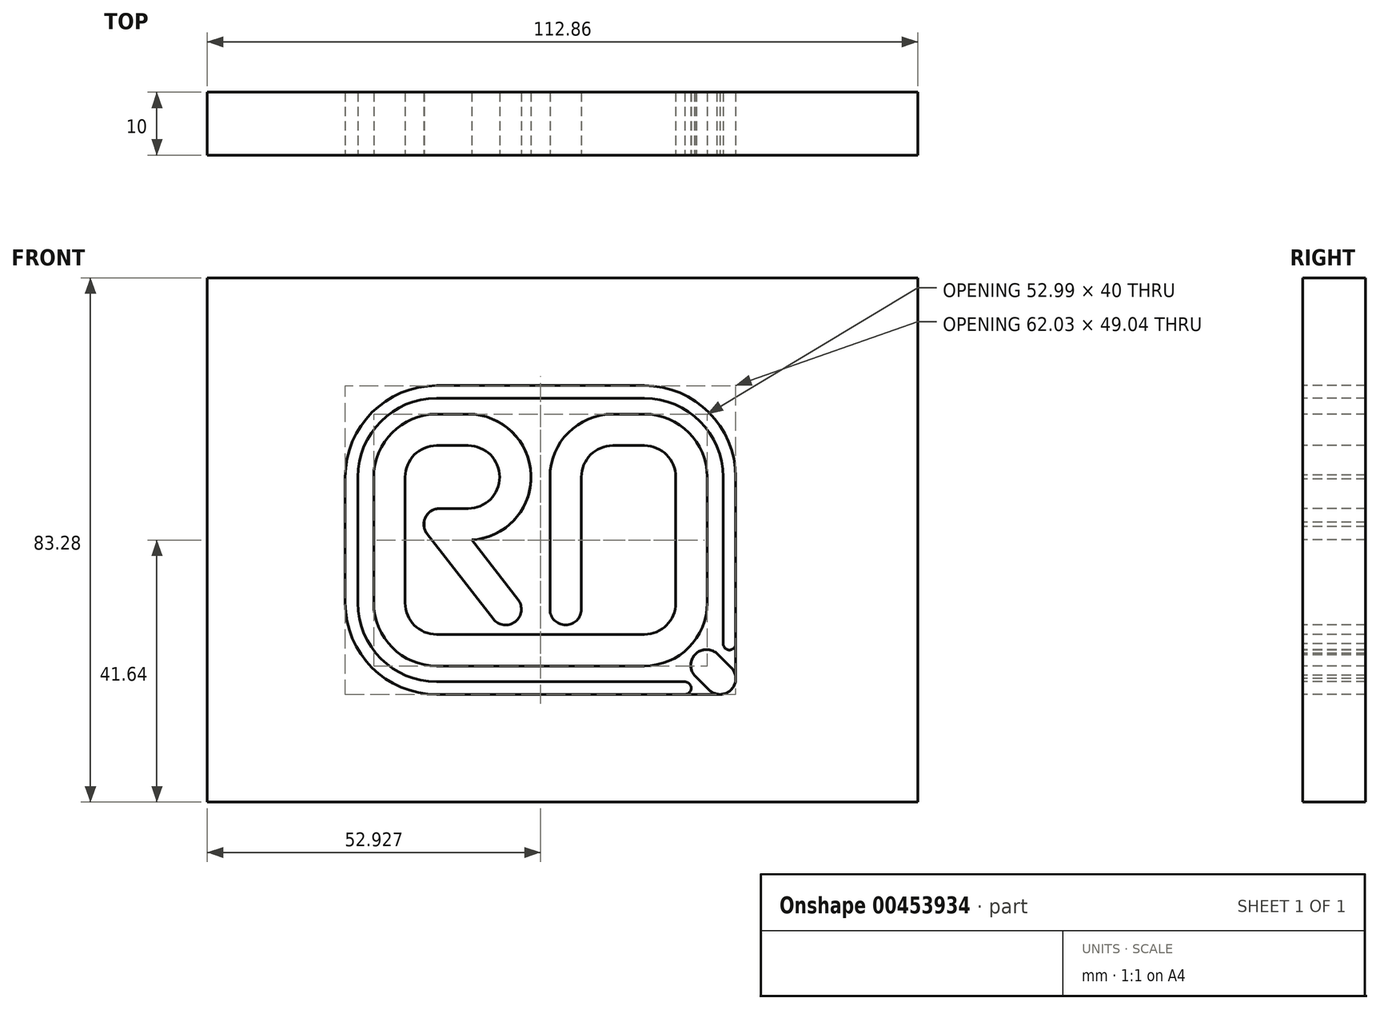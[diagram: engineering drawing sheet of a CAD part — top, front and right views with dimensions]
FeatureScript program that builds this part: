
annotation { "Feature Type Name" : "Feature", "Feature Type Description" : "" }
export const myFeature = defineFeature(function(context is Context, id is Id, definition is map)
    precondition{}
    {
        {
            var Q0;
            Q0=qCreatedBy(makeId("Front.planeOp"),FACE);
            var sketch = newSketch(context, id + "F0", { "sketchPlane" : qUnion([Q0])});
            skPoint(sketch, "E0.middle", {"position": v(0, 0) * mm});
            skLineSegment(sketch, "E1", {"start": v(-25, 10) * mm, "end": v(-25, -10) * mm});
            skLineSegment(sketch, "E2", {"start": v(-2, -20) * mm, "end": v(-0.38, -20) * mm});
            skLineSegment(sketch, "E3", {"start": v(-2, -11) * mm, "end": v(-2, 10) * mm});
            skLineSegment(sketch, "E4", {"start": v(8, 20) * mm, "end": v(13, 20) * mm});
            skLineSegment(sketch, "E5", {"start": v(23, 10) * mm, "end": v(23, -10) * mm});
            skLineSegment(sketch, "E6", {"start": v(13, -20) * mm, "end": v(9, -20) * mm});
            skLineSegment(sketch, "E7", {"start": v(-25, 20) * mm, "end": v(-15, 20) * mm});
            skLineSegment(sketch, "E8", {"start": v(-21, 0) * mm, "end": v(-15, 0) * mm, "construction": true});
            skLineSegment(sketch, "E9", {"start": v(-5, 10.33) * mm, "end": v(-5, 10.33) * mm});
            skPoint(sketch, "E10.visualSharp", {"position": v(-5.33, 20) * mm});
            skArc(sketch, "E10.filletArc", {"start": v(-5, 10.33) * mm, "mid": v(-8.05, 17.19) * mm, "end": v(-15, 20) * mm});
            skArc(sketch, "E11.filletArc", {"start": v(-15, 0) * mm, "mid": v(-7.81, 3.05) * mm, "end": v(-5, 10.33) * mm});
            skPoint(sketch, "E12.visualSharp", {"position": v(-3.63, -20) * mm});
            skPoint(sketch, "E13.visualSharp", {"position": v(23, -20) * mm});
            skArc(sketch, "E13.filletArc", {"start": v(13, -20) * mm, "mid": v(20.07, -17.07) * mm, "end": v(23, -10) * mm});
            skPoint(sketch, "E14.visualSharp", {"position": v(23, 20) * mm});
            skArc(sketch, "E14.filletArc", {"start": v(23, 10) * mm, "mid": v(20.07, 17.07) * mm, "end": v(13, 20) * mm});
            skPoint(sketch, "E15.visualSharp", {"position": v(-2, 20) * mm});
            skArc(sketch, "E15.filletArc", {"start": v(8, 20) * mm, "mid": v(0.92, 17.07) * mm, "end": v(-2, 10) * mm});
            skPoint(sketch, "E16.visualSharp", {"position": v(-2, -20) * mm});
            skArc(sketch, "E17.0", {"start": v(8, 15) * mm, "mid": v(4.46, 13.54) * mm, "end": v(3, 10) * mm});
            skLineSegment(sketch, "E17.1", {"start": v(3, -11) * mm, "end": v(3, 10) * mm});
            skLineSegment(sketch, "E17.2", {"start": v(8, 15) * mm, "end": v(13, 15) * mm});
            skArc(sketch, "E17.4", {"start": v(18, 10) * mm, "mid": v(16.53, 13.54) * mm, "end": v(13, 15) * mm});
            skLineSegment(sketch, "E17.5", {"start": v(18, 10) * mm, "end": v(18, -10) * mm});
            skArc(sketch, "E17.6", {"start": v(13, -15) * mm, "mid": v(16.53, -13.54) * mm, "end": v(18, -10) * mm});
            skLineSegment(sketch, "E17.7", {"start": v(13, -15) * mm, "end": v(9, -15) * mm});
            skArc(sketch, "E18.1", {"start": v(-15, 5) * mm, "mid": v(-11.44, 6.5) * mm, "end": v(-10, 10.08) * mm});
            skArc(sketch, "E18.2", {"start": v(-10, 10.08) * mm, "mid": v(-11.5, 13.56) * mm, "end": v(-15, 15) * mm});
            skLineSegment(sketch, "E18.3", {"start": v(-20, 15) * mm, "end": v(-15, 15) * mm});
            skLineSegment(sketch, "E19.0", {"start": v(-30, 17.5) * mm, "end": v(-30, -10) * mm});
            skLineSegment(sketch, "E20.0", {"start": v(-1, -15) * mm, "end": v(-0.38, -15) * mm});
            skLineSegment(sketch, "E21", {"start": v(-20, -20) * mm, "end": v(-2, -20) * mm});
            skLineSegment(sketch, "E22", {"start": v(-1, -15) * mm, "end": v(9, -15) * mm});
            skLineSegment(sketch, "E23.0", {"start": v(-20, -15) * mm, "end": v(0, -15) * mm});
            skLineSegment(sketch, "E24", {"start": v(-5, 10.33) * mm, "end": v(-5, 0) * mm});
            skLineSegment(sketch, "E25", {"start": v(0.5, -13.5) * mm, "end": v(0.5, -13.5) * mm});
            skPoint(sketch, "E26.visualSharp", {"position": v(3, -13.5) * mm});
            skArc(sketch, "E26.filletArc", {"start": v(0.5, -13.5) * mm, "mid": v(2.26, -12.77) * mm, "end": v(3, -11) * mm});
            skPoint(sketch, "E27.newPointB", {"position": v(-23.5, -13.5) * mm});
            skArc(sketch, "E27.filletArc", {"start": v(-2, -11) * mm, "mid": v(-1.27, -12.77) * mm, "end": v(0.5, -13.5) * mm});
            skPoint(sketch, "E28.visualSharp", {"position": v(-30, -20) * mm});
            skArc(sketch, "E28.filletArc", {"start": v(-30, -19.5) * mm, "mid": v(-29.85, -19.85) * mm, "end": v(-29.5, -20) * mm});
            skLineSegment(sketch, "E29", {"start": v(-7.28, -12.77) * mm, "end": v(-7.28, -12.77) * mm});
            skArc(sketch, "E30.filletArc", {"start": v(-7.28, -12.77) * mm, "mid": v(-6.55, -11) * mm, "end": v(-7.27, -9.24) * mm});
            skArc(sketch, "E31.filletArc", {"start": v(-11.23, -12.21) * mm, "mid": v(-9.4, -13.48) * mm, "end": v(-7.28, -12.77) * mm});
            skLineSegment(sketch, "E32.0", {"start": v(19.16, -19.7) * mm, "end": v(23.25, -23.79) * mm});
            skLineSegment(sketch, "E33.0", {"start": v(14.76, -15.3) * mm, "end": v(14.29, -14.83) * mm});
            skPoint(sketch, "E34.newPointB", {"position": v(-25, 20) * mm});
            skPoint(sketch, "E35.visualSharp", {"position": v(-23.5, 5) * mm});
            skPoint(sketch, "E36.visualSharp", {"position": v(-23.5, 0) * mm});
            skLineSegment(sketch, "E37", {"start": v(-30, 10) * mm, "end": v(-30, 17.5) * mm});
            skLineSegment(sketch, "E38", {"start": v(-20, 20) * mm, "end": v(-25, 20) * mm});
            skPoint(sketch, "E39.visualSharp", {"position": v(-30, 20) * mm});
            skArc(sketch, "E39.filletArc", {"start": v(-20, 20) * mm, "mid": v(-27.07, 17.07) * mm, "end": v(-30, 10) * mm});
            skArc(sketch, "E40", {"start": v(23.25, -23.79) * mm, "mid": v(26.79, -23.79) * mm, "end": v(26.78, -20.25) * mm});
            skPoint(sketch, "E41", {"position": v(20.07, -17.07) * mm});
            skPoint(sketch, "E42.orphan", {"position": v(16.53, -13.54) * mm});
            skLineSegment(sketch, "E43.trimOffspring", {"start": v(13, -20) * mm, "end": v(-0.38, -20) * mm});
            skArc(sketch, "E44.trimOffspring", {"start": v(19.16, -19.7) * mm, "mid": v(21.12, -18.14) * mm, "end": v(22.69, -16.19) * mm});
            skPoint(sketch, "E45.newPointB", {"position": v(-25, -20) * mm});
            skArc(sketch, "E45.filletArc", {"start": v(-25, -10) * mm, "mid": v(-23.54, -13.54) * mm, "end": v(-20, -15) * mm});
            skLineSegment(sketch, "E46", {"start": v(-15, 20) * mm, "end": v(8, 20) * mm});
            skLineSegment(sketch, "E47", {"start": v(21.86, -24.52) * mm, "end": v(-20, -24.52) * mm});
            skLineSegment(sketch, "E48", {"start": v(27.51, -22.02) * mm, "end": v(27.51, -18.87) * mm});
            skLineSegment(sketch, "E49", {"start": v(13, 24.52) * mm, "end": v(-20, 24.52) * mm});
            skLineSegment(sketch, "E50", {"start": v(-34.52, -10) * mm, "end": v(-34.52, 10) * mm});
            skPoint(sketch, "E51.orphan", {"position": v(17.43, -17.97) * mm});
            skPoint(sketch, "E52.orphan", {"position": v(13.35, -13.89) * mm});
            skArc(sketch, "E53.0", {"start": v(27.51, 10) * mm, "mid": v(23.26, 20.27) * mm, "end": v(13, 24.52) * mm});
            skArc(sketch, "E54.0", {"start": v(25.51, 10) * mm, "mid": v(21.85, 18.85) * mm, "end": v(13, 22.52) * mm});
            skLineSegment(sketch, "E55.0", {"start": v(25.51, -22.07) * mm, "end": v(25.51, -19) * mm});
            skLineSegment(sketch, "E56.0", {"start": v(25.02, -22.52) * mm, "end": v(21.98, -22.52) * mm});
            skLineSegment(sketch, "E57.0", {"start": v(-32.52, -10) * mm, "end": v(-32.52, 10) * mm});
            skLineSegment(sketch, "E58.0", {"start": v(13, 22.52) * mm, "end": v(-20, 22.52) * mm});
            skPoint(sketch, "E59.visualSharp", {"position": v(-32.52, 22.52) * mm});
            skArc(sketch, "E59.filletArc", {"start": v(-20, 22.52) * mm, "mid": v(-28.85, 18.85) * mm, "end": v(-32.52, 10) * mm});
            skArc(sketch, "E60.0", {"start": v(-20, 24.52) * mm, "mid": v(-30.27, 20.27) * mm, "end": v(-34.52, 10) * mm});
            skPoint(sketch, "E61.visualSharp", {"position": v(-32.52, -22.52) * mm});
            skLineSegment(sketch, "E62", {"start": v(26.51, -15) * mm, "end": v(26.51, -16.32) * mm});
            skLineSegment(sketch, "E63.0", {"start": v(18.1, -20.77) * mm, "end": v(22.19, -24.85) * mm, "construction": true});
            skLineSegment(sketch, "E64.0", {"start": v(23.75, -15.12) * mm, "end": v(27.84, -19.2) * mm, "construction": true});
            skArc(sketch, "E65", {"start": v(19.44, -24.52) * mm, "mid": v(20.44, -23.52) * mm, "end": v(19.44, -22.52) * mm});
            skArc(sketch, "E66", {"start": v(25.51, -16.47) * mm, "mid": v(26.51, -17.47) * mm, "end": v(27.51, -16.47) * mm});
            skLineSegment(sketch, "E67.trimOffspring", {"start": v(25.51, -14) * mm, "end": v(25.51, 10) * mm});
            skLineSegment(sketch, "E68.trimOffspring", {"start": v(27.51, -14) * mm, "end": v(27.51, 33) * mm});
            skLineSegment(sketch, "E69.trimOffspring", {"start": v(19.86, -22.52) * mm, "end": v(-20, -22.52) * mm});
            skLineSegment(sketch, "E70", {"start": v(21.86, -24.52) * mm, "end": v(25.02, -24.52) * mm});
            skLineSegment(sketch, "E71", {"start": v(27.51, -14) * mm, "end": v(27.51, -22.02) * mm});
            skLineSegment(sketch, "E72.bottom", {"start": v(-56.43, 41.64) * mm, "end": v(56.43, 41.64) * mm});
            skLineSegment(sketch, "E72.top", {"start": v(-56.43, -41.64) * mm, "end": v(56.43, -41.64) * mm});
            skLineSegment(sketch, "E72.left", {"start": v(-56.43, 41.64) * mm, "end": v(-56.43, -41.64) * mm});
            skLineSegment(sketch, "E72.right", {"start": v(56.43, 41.64) * mm, "end": v(56.43, -41.64) * mm});
            skLineSegment(sketch, "E73", {"start": v(0, 0) * mm, "end": v(0, -38.7) * mm, "construction": true});
            skLineSegment(sketch, "E74", {"start": v(0, 0) * mm, "end": v(33.56, 0) * mm, "construction": true});
            skArc(sketch, "E75.filletArc", {"start": v(-20, 15) * mm, "mid": v(-23.54, 13.54) * mm, "end": v(-25, 10) * mm});
            skArc(sketch, "E76.0", {"start": v(-30, -10) * mm, "mid": v(-27.07, -17.07) * mm, "end": v(-20, -20) * mm});
            skArc(sketch, "E77.0", {"start": v(-34.52, -10) * mm, "mid": v(-30.27, -20.27) * mm, "end": v(-20, -24.52) * mm});
            skArc(sketch, "E78.0", {"start": v(-32.52, -10) * mm, "mid": v(-28.85, -18.85) * mm, "end": v(-20, -22.52) * mm});
            skLineSegment(sketch, "E79", {"start": v(-15, 5) * mm, "end": v(-21, 5) * mm});
            skLineSegment(sketch, "E80", {"start": v(-23.5, 2.5) * mm, "end": v(-23.5, 2.5) * mm});
            skPoint(sketch, "E81.startSnap0", {"position": v(-6.55, -11) * mm});
            skArc(sketch, "E82.0", {"start": v(13, -22.52) * mm, "mid": v(21.85, -18.85) * mm, "end": v(25.51, -10) * mm});
            skArc(sketch, "E83", {"start": v(24.48, -17.98) * mm, "mid": v(21.11, -18.13) * mm, "end": v(20.96, -21.5) * mm});
            skLineSegment(sketch, "E84", {"start": v(24.48, -17.98) * mm, "end": v(26.78, -20.25) * mm});
            skLineSegment(sketch, "E85", {"start": v(25.51, -16.47) * mm, "end": v(25.51, -14) * mm});
            skLineSegment(sketch, "E86", {"start": v(-22, 7.18) * mm, "end": v(-22, -5.45) * mm});
            skArc(sketch, "E87", {"start": v(-19.53, 5) * mm, "mid": v(-22.03, 2.5) * mm, "end": v(-19.53, 0) * mm});
            skLineSegment(sketch, "E88", {"start": v(-21.5, 0.97) * mm, "end": v(-11.02, -12.53) * mm});
            skLineSegment(sketch, "E89.0", {"start": v(-17.54, 4.02) * mm, "end": v(-7.07, -9.47) * mm});
            skSolve(sketch);
        }
        {
            var Q0;
            Q0=makeQuery(id+"F0.imprint","IMPRINT",FACE,{"disambiguationData":[TD([[makeQuery(id+"F0.imprint","IMPRINT",EDGE,{"derivedFrom":sQuery(id+"F0.wireOp",EDGE,"E1")}),-1.0]])]});
            var Q1;
            {var subQ6=sQuery(id+"F0.wireOp",EDGE,"8dgEX87s-OnN3-UPAw-RyUf-tcfM0RuKeMZf");Q1=makeQuery(id+"F0.imprint","IMPRINT",FACE,{"disambiguationData":[TD([[makeQuery(id+"F0.imprint","IMPRINT",EDGE,{"derivedFrom":subQ6}),1.0]])]});}
            var Q2;
            {var subQ0=sQuery(id+"F0.wireOp",EDGE,"E40");var subQ1=makeQuery(id+"F0.imprint","INTERSECT",VERTEX,{"derivedFrom":[sQuery(id+"F0.wireOp",EDGE,"c0c087a9-fd36-4214-a694-875f0f01d769.0"),subQ0]});Q2=makeQuery(id+"F0.imprint","IMPRINT",FACE,{"disambiguationData":[TD([[makeQuery(id+"F0.imprint","IMPRINT",EDGE,{"disambiguationData":[TD([[subQ1,-1.0]])],"derivedFrom":subQ0}),1.0]])]});}
            var Q3;
            {var subQ0=sQuery(id+"F0.wireOp",EDGE,"E0.bottom");Q3=makeQuery(id+"F0.imprint","IMPRINT",FACE,{"disambiguationData":[TD([[makeQuery(id+"F0.imprint","IMPRINT",EDGE,{"derivedFrom":subQ0}),-1.0]])]});}
            var Q4;
            {var subQ0=sQuery(id+"F0.wireOp",EDGE,"E0.bottom");Q4=makeQuery(id+"F0.imprint","IMPRINT",FACE,{"disambiguationData":[TD([[makeQuery(id+"F0.imprint","IMPRINT",EDGE,{"derivedFrom":subQ0}),1.0]])]});}
            var Q5;
            {var subQ0=sQuery(id+"F0.wireOp",EDGE,"E31.filletArc");Q5=makeQuery(id+"F0.imprint","IMPRINT",FACE,{"disambiguationData":[TD([[makeQuery(id+"F0.imprint","IMPRINT",EDGE,{"derivedFrom":subQ0}),1.0]])]});}
            var Q6;
            {var subQ0=sQuery(id+"F0.wireOp",EDGE,"E83");var subQ1=sQuery(id+"F0.wireOp",EDGE,"E44.trimOffspring");var subQ2=makeQuery(id+"F0.imprint","INTERSECT",VERTEX,{"disambiguationData":[OD(0.0)],"derivedFrom":[subQ1,subQ0]});Q6=makeQuery(id+"F0.imprint","IMPRINT",FACE,{"disambiguationData":[TD([[makeQuery(id+"F0.imprint","IMPRINT",EDGE,{"disambiguationData":[TD([[subQ2,-1.0]])],"derivedFrom":subQ1}),-1.0]])]});}
            var Q7;
            {var subQ6=sQuery(id+"F0.wireOp",EDGE,"E32.0");var subQ8=makeQuery(id+"F0.imprint","IMPRINT",VERTEX,{"derivedFrom":subQ6});Q7=makeQuery(id+"F0.imprint","IMPRINT",FACE,{"disambiguationData":[TD([[makeQuery(id+"F0.imprint","IMPRINT",EDGE,{"disambiguationData":[TD([[subQ8,1.0]])],"derivedFrom":subQ6}),1.0]])]});}
            var Q8;
            {var subQ0=sQuery(id+"F0.wireOp",EDGE,"E83");var subQ1=sQuery(id+"F0.wireOp",EDGE,"E44.trimOffspring");var subQ2=makeQuery(id+"F0.imprint","INTERSECT",VERTEX,{"disambiguationData":[OD(0.0)],"derivedFrom":[subQ1,subQ0]});Q8=makeQuery(id+"F0.imprint","IMPRINT",FACE,{"disambiguationData":[TD([[makeQuery(id+"F0.imprint","IMPRINT",EDGE,{"disambiguationData":[TD([[subQ2,1.0]])],"derivedFrom":subQ1}),-1.0]])]});}
            extrude(context, id + "F1", {"entities" : qUnion([Q0, Q1, Q2, Q3, Q4, Q5, Q6, Q7, Q8]), "oppositeDirection" : true, "depth" : 10 * mm});
        }
        {
            var Q0;
            Q0=makeQuery(id+"F0.imprint","IMPRINT",FACE,{"disambiguationData":[TD([[makeQuery(id+"F0.imprint","IMPRINT",EDGE,{"derivedFrom":sQuery(id+"F0.wireOp",EDGE,"E1")}),1.0]])]});
            var Q1;
            {var subQ16=sQuery(id+"F0.wireOp",EDGE,"E2");Q1=makeQuery(id+"F0.imprint","IMPRINT",FACE,{"disambiguationData":[TD([[makeQuery(id+"F0.imprint","IMPRINT",EDGE,{"derivedFrom":subQ16}),-1.0]])]});}
            var Q2;
            {var subQ10=sQuery(id+"F0.wireOp",EDGE,"E65");Q2=makeQuery(id+"F0.imprint","IMPRINT",FACE,{"disambiguationData":[TD([[makeQuery(id+"F0.imprint","IMPRINT",EDGE,{"derivedFrom":subQ10}),-1.0]])]});}
            var Q3;
            {var subQ0=sQuery(id+"F0.wireOp",EDGE,"E44.trimOffspring");var subQ1=sQuery(id+"F0.wireOp",EDGE,"E32.0");var subQ2=makeQuery(id+"F0.imprint","INTERSECT",VERTEX,{"derivedFrom":[subQ1,subQ0]});Q3=makeQuery(id+"F0.imprint","IMPRINT",FACE,{"disambiguationData":[TD([[makeQuery(id+"F0.imprint","IMPRINT",EDGE,{"disambiguationData":[TD([[subQ2,-1.0]])],"derivedFrom":subQ1}),1.0]])]});}
            var Q4;
            {var subQ0=sQuery(id+"F0.wireOp",EDGE,"E83");var subQ1=sQuery(id+"F0.wireOp",EDGE,"E32.0");var subQ2=makeQuery(id+"F0.imprint","INTERSECT",VERTEX,{"derivedFrom":[subQ1,subQ0]});Q4=makeQuery(id+"F0.imprint","IMPRINT",FACE,{"disambiguationData":[TD([[makeQuery(id+"F0.imprint","IMPRINT",EDGE,{"disambiguationData":[TD([[subQ2,1.0]])],"derivedFrom":subQ1}),1.0]])]});}
            var Q5;
            {var subQ1=sQuery(id+"F0.wireOp",EDGE,"E66");Q5=makeQuery(id+"F0.imprint","IMPRINT",FACE,{"disambiguationData":[TD([[makeQuery(id+"F0.imprint","IMPRINT",EDGE,{"derivedFrom":subQ1}),-1.0]])]});}
            extrude(context, id + "F2", {"entities" : qUnion([Q0, Q1, Q2, Q3, Q4, Q5]), "oppositeDirection" : true, "depth" : 10 * mm});
        }
        {
            var Q0;
            Q0=makeQuery(id+"F0.imprint","IMPRINT",FACE,{"disambiguationData":[TD([[makeQuery(id+"F0.imprint","IMPRINT",EDGE,{"derivedFrom":sQuery(id+"F0.wireOp",EDGE,"E49")}),-1.0]])]});
            extrude(context, id + "F3", {"entities" : qUnion([Q0]), "oppositeDirection" : true, "depth" : 10 * mm});
        }
        {
            var Q0;
            Q0=makeQuery(id+"F0.imprint","IMPRINT",FACE,{"disambiguationData":[TD([[makeQuery(id+"F0.imprint","IMPRINT",EDGE,{"derivedFrom":sQuery(id+"F0.wireOp",EDGE,"E49")}),1.0]])]});
            var Q1;
            {var subQ0=sQuery(id+"F0.wireOp",EDGE,"E65");var subQ2=makeQuery(id+"F0.imprint","IMPRINT",VERTEX,{"derivedFrom":subQ0});Q1=makeQuery(id+"F0.imprint","IMPRINT",FACE,{"disambiguationData":[TD([[makeQuery(id+"F0.imprint","IMPRINT",EDGE,{"disambiguationData":[TD([[subQ2,-1.0]])],"derivedFrom":subQ0}),1.0]])]});}
            var Q2;
            {var subQ0=sQuery(id+"F0.wireOp",EDGE,"E66");var subQ3=makeQuery(id+"F0.imprint","IMPRINT",VERTEX,{"derivedFrom":subQ0});Q2=makeQuery(id+"F0.imprint","IMPRINT",FACE,{"disambiguationData":[TD([[makeQuery(id+"F0.imprint","IMPRINT",EDGE,{"disambiguationData":[TD([[subQ3,1.0]])],"derivedFrom":subQ0}),1.0]])]});}
            extrude(context, id + "F4", {"entities" : qUnion([Q0, Q1, Q2]), "oppositeDirection" : true, "depth" : 10 * mm});
        }
    });
